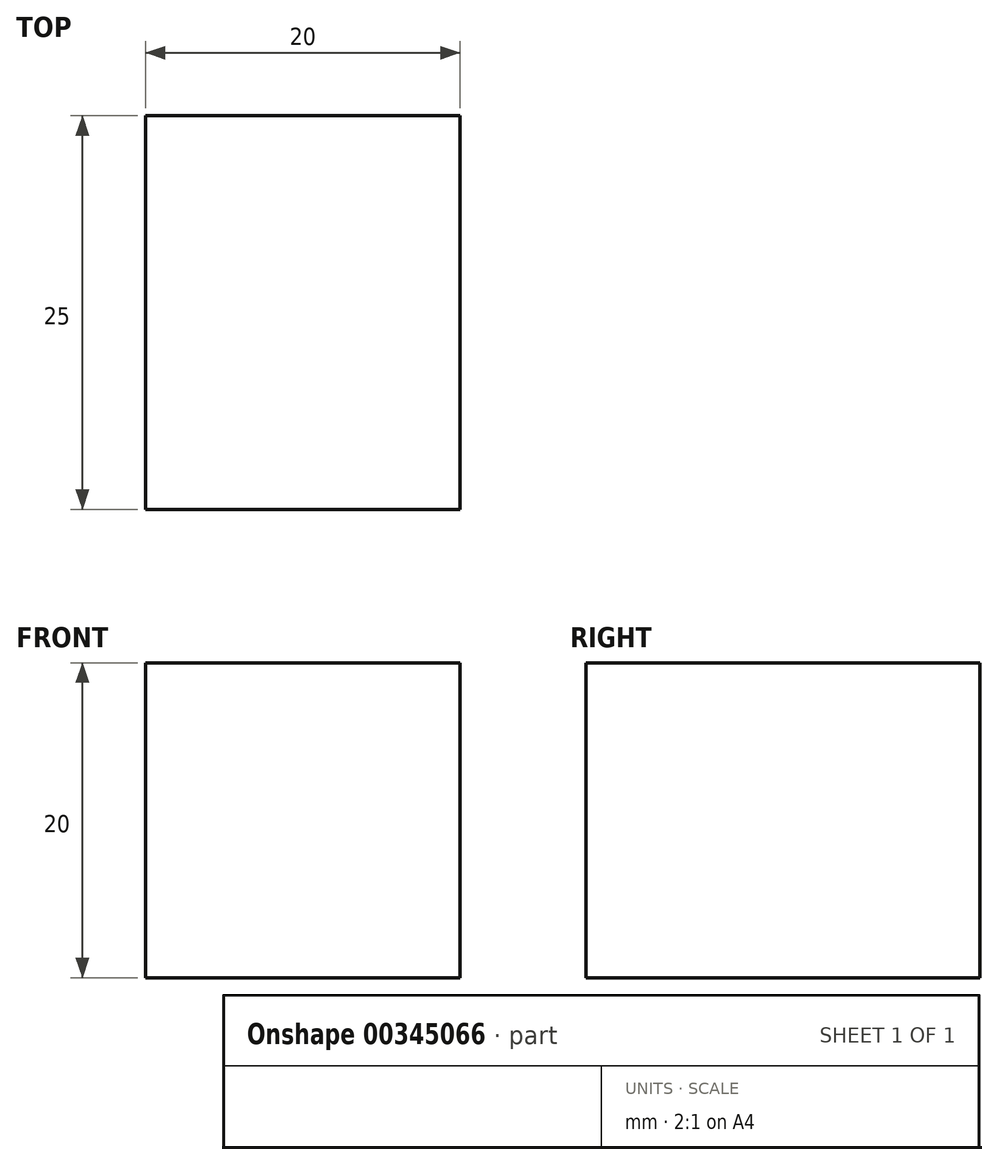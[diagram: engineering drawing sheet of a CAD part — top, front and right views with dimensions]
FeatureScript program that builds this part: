
annotation { "Feature Type Name" : "Feature", "Feature Type Description" : "" }
export const myFeature = defineFeature(function(context is Context, id is Id, definition is map)
    precondition{}
    {
        {
            var Q0;
            Q0=qCreatedBy(makeId("Front.planeOp"),FACE);
            var sketch = newSketch(context, id + "F0", { "sketchPlane" : qUnion([Q0])});
            skLineSegment(sketch, "E0.bottom", {"start": v(-8.73, 10) * mm, "end": v(11.27, 10) * mm});
            skLineSegment(sketch, "E0.top", {"start": v(-8.73, -10) * mm, "end": v(11.27, -10) * mm});
            skLineSegment(sketch, "E0.left", {"start": v(-8.73, 10) * mm, "end": v(-8.73, -10) * mm});
            skLineSegment(sketch, "E0.right", {"start": v(11.27, 10) * mm, "end": v(11.27, -10) * mm});
            skSolve(sketch);
        }
        {
            var Q0;
            Q0 = qSketchRegion(id + "F0", true);
            extrude(context, id + "F1", {"entities" : qUnion([Q0]), "depth" : 25 * mm});
        }
    });
